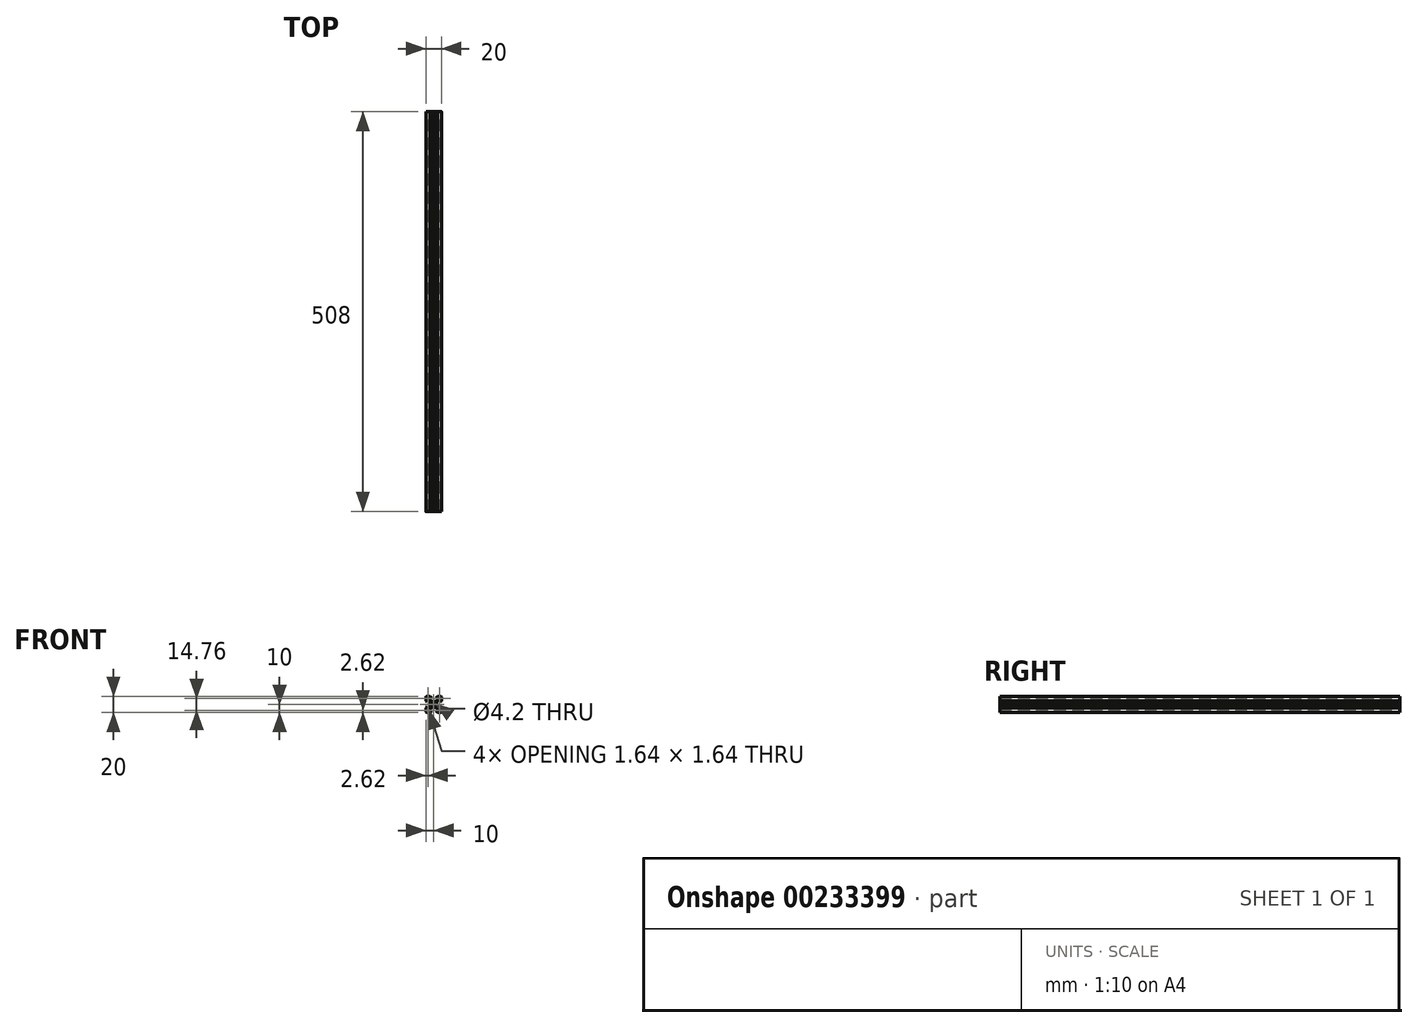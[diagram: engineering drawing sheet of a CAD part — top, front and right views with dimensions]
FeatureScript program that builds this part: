
annotation { "Feature Type Name" : "Feature", "Feature Type Description" : "" }
export const myFeature = defineFeature(function(context is Context, id is Id, definition is map)
    precondition{}
    {
        {
            var Q0;
            Q0=qCreatedBy(makeId("Front.planeOp"),FACE);
            var sketch = newSketch(context, id + "F0", { "sketchPlane" : qUnion([Q0])});
            skLineSegment(sketch, "E0.rect.bottom", {"start": v(-9, 10) * mm, "end": v(9, 10) * mm});
            skLineSegment(sketch, "E0.rect.top", {"start": v(-9, -10) * mm, "end": v(9, -10) * mm});
            skLineSegment(sketch, "E0.rect.left", {"start": v(-10, 9) * mm, "end": v(-10, -9) * mm});
            skLineSegment(sketch, "E0.rect.right", {"start": v(10, 9) * mm, "end": v(10, -9) * mm});
            skPoint(sketch, "E0.rect.middle", {"position": v(0, 0) * mm});
            skCircle(sketch, "E1", {"center": v(0, 0) * mm, "radius": 2.1 * mm});
            skPoint(sketch, "E2.visualSharp", {"position": v(-10, 10) * mm});
            skArc(sketch, "E2.filletArc", {"start": v(-9, 10) * mm, "mid": v(-9.7, 9.7) * mm, "end": v(-10, 9) * mm});
            skPoint(sketch, "E3.visualSharp", {"position": v(10, 10) * mm});
            skArc(sketch, "E3.filletArc", {"start": v(10, 9) * mm, "mid": v(9.7, 9.7) * mm, "end": v(9, 10) * mm});
            skPoint(sketch, "E4.visualSharp", {"position": v(10, -10) * mm});
            skArc(sketch, "E4.filletArc", {"start": v(9, -10) * mm, "mid": v(9.7, -9.7) * mm, "end": v(10, -9) * mm});
            skPoint(sketch, "E5.visualSharp", {"position": v(-10, -10) * mm});
            skArc(sketch, "E5.filletArc", {"start": v(-10, -9) * mm, "mid": v(-9.7, -9.7) * mm, "end": v(-9, -10) * mm});
            skLineSegment(sketch, "E6", {"start": v(10, 10) * mm, "end": v(-10, -10) * mm, "construction": true});
            skLineSegment(sketch, "E7", {"start": v(-10, 10) * mm, "end": v(10, -10) * mm, "construction": true});
            skLineSegment(sketch, "E8", {"start": v(-4.64, 10) * mm, "end": v(-2.84, 8.2) * mm});
            skLineSegment(sketch, "E9", {"start": v(-2.84, 8.2) * mm, "end": v(-5.5, 8.2) * mm});
            skLineSegment(sketch, "E10", {"start": v(-5.5, 8.2) * mm, "end": v(-5.5, 6.56) * mm});
            skLineSegment(sketch, "E11", {"start": v(-5.5, 6.56) * mm, "end": v(-2.84, 3.9) * mm});
            skLineSegment(sketch, "E12.MirrorCS", {"start": v(4.64, 10) * mm, "end": v(2.84, 8.2) * mm});
            skLineSegment(sketch, "E13.MirrorCS", {"start": v(2.84, 8.2) * mm, "end": v(5.5, 8.2) * mm});
            skLineSegment(sketch, "E14.MirrorCS", {"start": v(5.5, 8.2) * mm, "end": v(5.5, 6.56) * mm});
            skLineSegment(sketch, "E15.MirrorCS", {"start": v(5.5, 6.56) * mm, "end": v(2.84, 3.9) * mm});
            skLineSegment(sketch, "E16", {"start": v(-2.84, 3.9) * mm, "end": v(2.84, 3.9) * mm});
            skLineSegment(sketch, "E17.MirrorCS", {"start": v(-4.64, -10) * mm, "end": v(-2.84, -8.2) * mm});
            skLineSegment(sketch, "E18.MirrorCS", {"start": v(-2.84, -8.2) * mm, "end": v(-5.5, -8.2) * mm});
            skLineSegment(sketch, "E19.MirrorCS", {"start": v(-5.5, -8.2) * mm, "end": v(-5.5, -6.56) * mm});
            skLineSegment(sketch, "E20.MirrorCS", {"start": v(-5.5, -6.56) * mm, "end": v(-2.84, -3.9) * mm});
            skLineSegment(sketch, "E21.MirrorCS", {"start": v(-2.84, -3.9) * mm, "end": v(2.84, -3.9) * mm});
            skLineSegment(sketch, "E22.MirrorCS", {"start": v(5.5, -6.56) * mm, "end": v(2.84, -3.9) * mm});
            skLineSegment(sketch, "E23.MirrorCS", {"start": v(5.5, -8.2) * mm, "end": v(5.5, -6.56) * mm});
            skLineSegment(sketch, "E24.MirrorCS", {"start": v(2.84, -8.2) * mm, "end": v(5.5, -8.2) * mm});
            skLineSegment(sketch, "E25.MirrorCS", {"start": v(4.64, -10) * mm, "end": v(2.84, -8.2) * mm});
            skLineSegment(sketch, "E26.MirrorCS", {"start": v(10, -4.64) * mm, "end": v(8.2, -2.84) * mm});
            skLineSegment(sketch, "E27.MirrorCS", {"start": v(8.2, -2.84) * mm, "end": v(8.2, -5.5) * mm});
            skLineSegment(sketch, "E28.MirrorCS", {"start": v(8.2, -5.5) * mm, "end": v(6.56, -5.5) * mm});
            skLineSegment(sketch, "E29.MirrorCS", {"start": v(6.56, -5.5) * mm, "end": v(3.9, -2.84) * mm});
            skLineSegment(sketch, "E30.MirrorCS", {"start": v(3.9, -2.84) * mm, "end": v(3.9, 2.84) * mm});
            skLineSegment(sketch, "E31.MirrorCS", {"start": v(6.56, 5.5) * mm, "end": v(3.9, 2.84) * mm});
            skLineSegment(sketch, "E32.MirrorCS", {"start": v(8.2, 5.5) * mm, "end": v(6.56, 5.5) * mm});
            skLineSegment(sketch, "E33.MirrorCS", {"start": v(8.2, 2.84) * mm, "end": v(8.2, 5.5) * mm});
            skLineSegment(sketch, "E34.MirrorCS", {"start": v(10, 4.64) * mm, "end": v(8.2, 2.84) * mm});
            skLineSegment(sketch, "E35.MirrorCS", {"start": v(-8.2, 2.84) * mm, "end": v(-8.2, 5.5) * mm});
            skLineSegment(sketch, "E36.MirrorCS", {"start": v(-10, 4.64) * mm, "end": v(-8.2, 2.84) * mm});
            skLineSegment(sketch, "E37.MirrorCS", {"start": v(-8.2, 5.5) * mm, "end": v(-6.56, 5.5) * mm});
            skLineSegment(sketch, "E38.MirrorCS", {"start": v(-6.56, 5.5) * mm, "end": v(-3.9, 2.84) * mm});
            skLineSegment(sketch, "E39.MirrorCS", {"start": v(-3.9, 2.84) * mm, "end": v(-3.9, -2.84) * mm});
            skLineSegment(sketch, "E40.MirrorCS", {"start": v(-6.56, -5.5) * mm, "end": v(-3.9, -2.84) * mm});
            skLineSegment(sketch, "E41.MirrorCS", {"start": v(-8.2, -5.5) * mm, "end": v(-6.56, -5.5) * mm});
            skLineSegment(sketch, "E42.MirrorCS", {"start": v(-8.2, -2.84) * mm, "end": v(-8.2, -5.5) * mm});
            skLineSegment(sketch, "E43.MirrorCS", {"start": v(-10, -4.64) * mm, "end": v(-8.2, -2.84) * mm});
            skLineSegment(sketch, "E44", {"start": v(-8.05, 8.2) * mm, "end": v(-6.71, 8.2) * mm});
            skLineSegment(sketch, "E45", {"start": v(-6.56, 8.05) * mm, "end": v(-6.56, 8.05) * mm});
            skLineSegment(sketch, "E46", {"start": v(-6.6, 7.94) * mm, "end": v(-7.94, 6.6) * mm});
            skLineSegment(sketch, "E47", {"start": v(-8.05, 6.56) * mm, "end": v(-8.05, 6.56) * mm});
            skLineSegment(sketch, "E48", {"start": v(-8.2, 6.7) * mm, "end": v(-8.2, 8.05) * mm});
            skLineSegment(sketch, "E49.MirrorCS", {"start": v(8.2, 6.71) * mm, "end": v(8.2, 8.05) * mm});
            skLineSegment(sketch, "E50.MirrorCS", {"start": v(7.99, 6.56) * mm, "end": v(8.05, 6.56) * mm});
            skLineSegment(sketch, "E51.MirrorCS", {"start": v(6.56, 7.99) * mm, "end": v(7.99, 6.56) * mm});
            skLineSegment(sketch, "E52.MirrorCS", {"start": v(6.56, 8.05) * mm, "end": v(6.56, 7.99) * mm});
            skLineSegment(sketch, "E53.MirrorCS", {"start": v(8.05, 8.2) * mm, "end": v(6.7, 8.2) * mm});
            skLineSegment(sketch, "E54.MirrorCS", {"start": v(-8.2, -6.7) * mm, "end": v(-8.2, -8.2) * mm});
            skLineSegment(sketch, "E55.MirrorCS", {"start": v(-7.99, -6.56) * mm, "end": v(-8.05, -6.56) * mm});
            skLineSegment(sketch, "E56.MirrorCS", {"start": v(-6.6, -7.94) * mm, "end": v(-7.99, -6.56) * mm});
            skLineSegment(sketch, "E57.MirrorCS", {"start": v(-6.56, -8.05) * mm, "end": v(-6.56, -8.05) * mm});
            skLineSegment(sketch, "E58.MirrorCS", {"start": v(-8.2, -8.2) * mm, "end": v(-6.7, -8.2) * mm});
            skLineSegment(sketch, "E59.MirrorCS", {"start": v(6.56, -8.05) * mm, "end": v(6.56, -7.99) * mm});
            skLineSegment(sketch, "E60.MirrorCS", {"start": v(6.56, -7.99) * mm, "end": v(7.94, -6.6) * mm});
            skLineSegment(sketch, "E61.MirrorCS", {"start": v(8.05, -6.56) * mm, "end": v(8.2, -6.56) * mm});
            skLineSegment(sketch, "E62.MirrorCS", {"start": v(8.2, -6.56) * mm, "end": v(8.2, -8.05) * mm});
            skLineSegment(sketch, "E63.MirrorCS", {"start": v(8.05, -8.2) * mm, "end": v(6.7, -8.2) * mm});
            skLineSegment(sketch, "E64", {"start": v(-0.15, 3.9) * mm, "end": v(0, 3.75) * mm});
            skLineSegment(sketch, "E65", {"start": v(0, 3.75) * mm, "end": v(0.15, 3.9) * mm});
            skLineSegment(sketch, "E66.MirrorCS", {"start": v(-0.15, -3.9) * mm, "end": v(0, -3.75) * mm});
            skLineSegment(sketch, "E67.MirrorCS", {"start": v(0, -3.75) * mm, "end": v(0.15, -3.9) * mm});
            skLineSegment(sketch, "E68.MirrorCS", {"start": v(3.9, -0.15) * mm, "end": v(3.75, 0) * mm});
            skLineSegment(sketch, "E69.MirrorCS", {"start": v(3.75, 0) * mm, "end": v(3.9, 0.15) * mm});
            skLineSegment(sketch, "E70.MirrorCS", {"start": v(-3.9, 0.15) * mm, "end": v(-3.75, 0) * mm});
            skLineSegment(sketch, "E71.MirrorCS", {"start": v(-3.75, 0) * mm, "end": v(-3.9, -0.15) * mm});
            skPoint(sketch, "E72.visualSharp", {"position": v(-8.2, 8.2) * mm});
            skArc(sketch, "E72.filletArc", {"start": v(-8.05, 8.2) * mm, "mid": v(-8.16, 8.16) * mm, "end": v(-8.2, 8.05) * mm});
            skPoint(sketch, "E73.visualSharp", {"position": v(-6.56, 7.99) * mm});
            skArc(sketch, "E73.filletArc", {"start": v(-6.6, 7.94) * mm, "mid": v(-6.57, 8) * mm, "end": v(-6.56, 8.05) * mm});
            skPoint(sketch, "E74.visualSharp", {"position": v(-7.99, 6.56) * mm});
            skArc(sketch, "E74.filletArc", {"start": v(-8.05, 6.56) * mm, "mid": v(-8, 6.57) * mm, "end": v(-7.94, 6.6) * mm});
            skPoint(sketch, "E75.visualSharp", {"position": v(-6.56, 8.2) * mm});
            skArc(sketch, "E75.filletArc", {"start": v(-6.56, 8.05) * mm, "mid": v(-6.6, 8.16) * mm, "end": v(-6.71, 8.2) * mm});
            skPoint(sketch, "E76.visualSharp", {"position": v(-8.2, 6.56) * mm});
            skArc(sketch, "E76.filletArc", {"start": v(-8.2, 6.7) * mm, "mid": v(-8.16, 6.6) * mm, "end": v(-8.05, 6.56) * mm});
            skPoint(sketch, "E77.visualSharp", {"position": v(6.56, 8.2) * mm});
            skArc(sketch, "E77.filletArc", {"start": v(6.7, 8.2) * mm, "mid": v(6.6, 8.16) * mm, "end": v(6.56, 8.05) * mm});
            skPoint(sketch, "E78.visualSharp", {"position": v(8.2, 8.2) * mm});
            skArc(sketch, "E78.filletArc", {"start": v(8.2, 8.05) * mm, "mid": v(8.16, 8.16) * mm, "end": v(8.05, 8.2) * mm});
            skPoint(sketch, "E79.visualSharp", {"position": v(8.2, 6.56) * mm});
            skArc(sketch, "E79.filletArc", {"start": v(8.05, 6.56) * mm, "mid": v(8.16, 6.6) * mm, "end": v(8.2, 6.71) * mm});
            skPoint(sketch, "E80.visualSharp", {"position": v(6.56, -8.2) * mm});
            skArc(sketch, "E80.filletArc", {"start": v(6.56, -8.05) * mm, "mid": v(6.6, -8.16) * mm, "end": v(6.7, -8.2) * mm});
            skPoint(sketch, "E81.visualSharp", {"position": v(7.99, -6.56) * mm});
            skArc(sketch, "E81.filletArc", {"start": v(8.05, -6.56) * mm, "mid": v(8, -6.57) * mm, "end": v(7.94, -6.6) * mm});
            skPoint(sketch, "E82.visualSharp", {"position": v(8.2, -8.2) * mm});
            skArc(sketch, "E82.filletArc", {"start": v(8.05, -8.2) * mm, "mid": v(8.16, -8.16) * mm, "end": v(8.2, -8.05) * mm});
            skPoint(sketch, "E83.visualSharp", {"position": v(-6.56, -8.2) * mm});
            skArc(sketch, "E83.filletArc", {"start": v(-6.7, -8.2) * mm, "mid": v(-6.6, -8.16) * mm, "end": v(-6.56, -8.05) * mm});
            skPoint(sketch, "E84.visualSharp", {"position": v(-8.2, -6.56) * mm});
            skArc(sketch, "E84.filletArc", {"start": v(-8.05, -6.56) * mm, "mid": v(-8.16, -6.6) * mm, "end": v(-8.2, -6.7) * mm});
            skPoint(sketch, "E85.visualSharp", {"position": v(-6.56, -7.99) * mm});
            skArc(sketch, "E85.filletArc", {"start": v(-6.56, -8.05) * mm, "mid": v(-6.57, -8) * mm, "end": v(-6.6, -7.94) * mm});
            skSolve(sketch);
        }
        {
            var Q0;
            Q0=makeQuery(id+"F0.imprint","IMPRINT",FACE,{"disambiguationData":[TD([[makeQuery(id+"F0.imprint","IMPRINT",EDGE,{"derivedFrom":sQuery(id+"F0.wireOp",EDGE,"E1")}),-1.0]])]});
            extrude(context, id + "F1", {"entities" : qUnion([Q0]), "depth" : 508 * mm});
        }
    });
